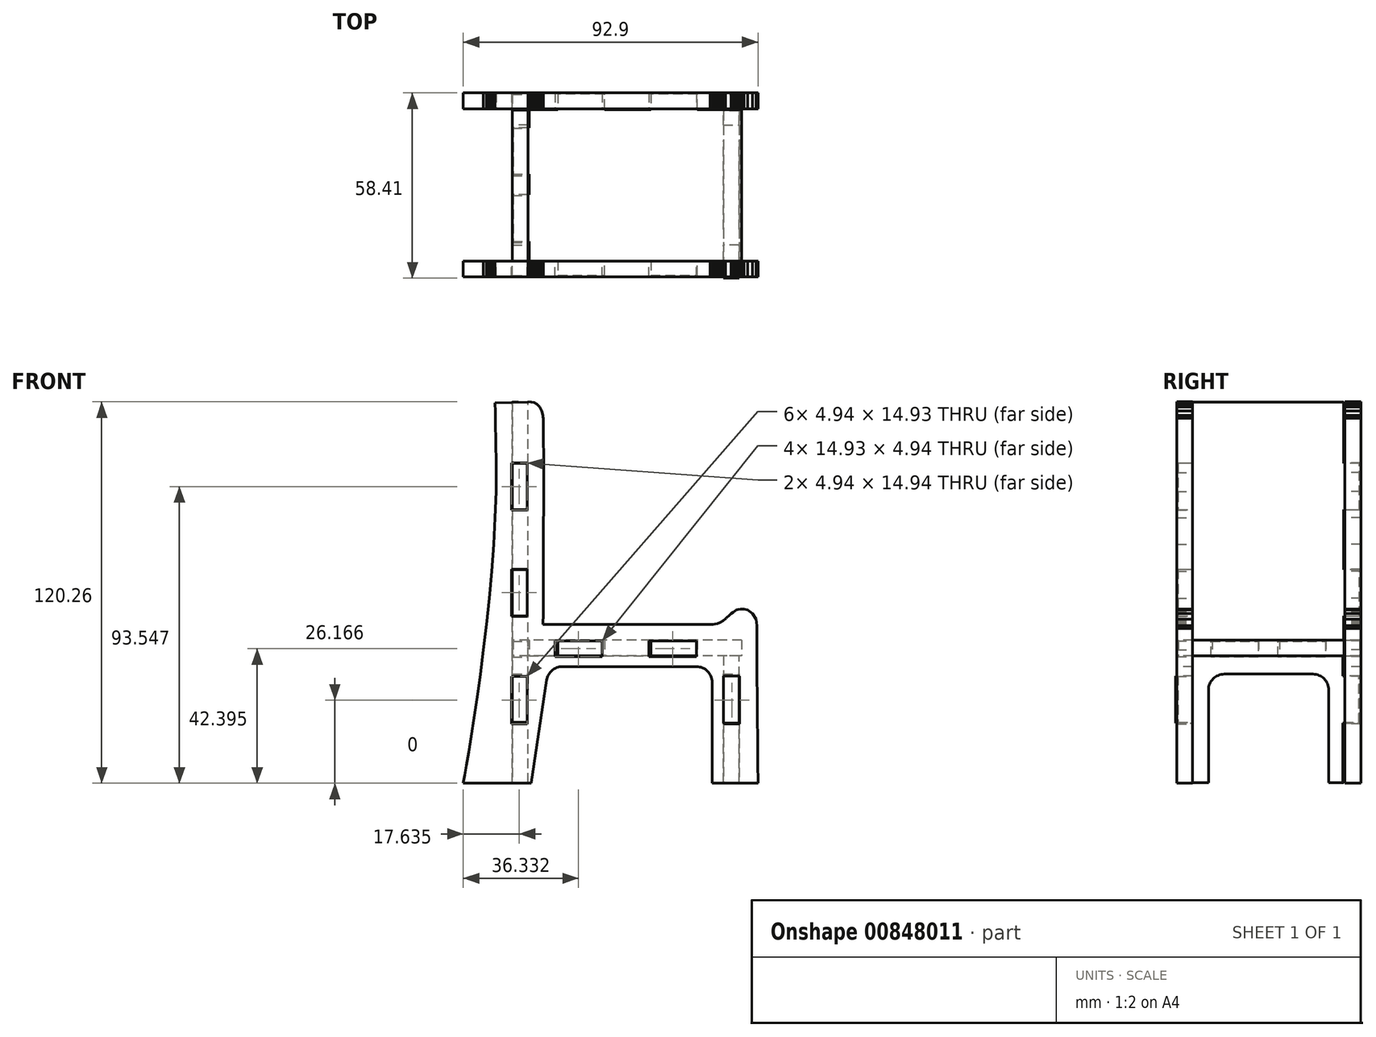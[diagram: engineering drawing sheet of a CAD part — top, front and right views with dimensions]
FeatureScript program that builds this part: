
annotation { "Feature Type Name" : "Feature", "Feature Type Description" : "" }
export const myFeature = defineFeature(function(context is Context, id is Id, definition is map)
    precondition{}
    {
        {
            var Q0;
            Q0=qCreatedBy(makeId("Front.planeOp"),FACE);
            var sketch = newSketch(context, id + "F0", { "sketchPlane" : qUnion([Q0])});
            skLineSegment(sketch, "E0", {"start": v(-31.28, -26.5) * mm, "end": v(-26.35, -26.5) * mm});
            skLineSegment(sketch, "E1", {"start": v(-26.35, -26.5) * mm, "end": v(-26.35, -41.43) * mm});
            skLineSegment(sketch, "E2", {"start": v(-26.35, -41.43) * mm, "end": v(-31.28, -41.43) * mm});
            skLineSegment(sketch, "E3", {"start": v(-31.28, -41.43) * mm, "end": v(-31.28, -26.5) * mm});
            skLineSegment(sketch, "E4", {"start": v(-31.28, 7.37) * mm, "end": v(-26.35, 7.37) * mm});
            skLineSegment(sketch, "E5", {"start": v(-26.35, 7.37) * mm, "end": v(-26.35, -7.56) * mm});
            skLineSegment(sketch, "E6", {"start": v(-26.35, -7.56) * mm, "end": v(-31.28, -7.56) * mm});
            skLineSegment(sketch, "E7", {"start": v(-31.28, -7.56) * mm, "end": v(-31.28, 7.37) * mm});
            skLineSegment(sketch, "E8", {"start": v(-31.28, 40.88) * mm, "end": v(-26.35, 40.88) * mm});
            skLineSegment(sketch, "E9", {"start": v(-26.35, 40.88) * mm, "end": v(-26.35, 25.95) * mm});
            skLineSegment(sketch, "E10", {"start": v(-26.35, 25.95) * mm, "end": v(-31.28, 25.95) * mm});
            skLineSegment(sketch, "E11", {"start": v(-31.28, 25.95) * mm, "end": v(-31.28, 40.88) * mm});
            skLineSegment(sketch, "E12", {"start": v(-17.59, -15.27) * mm, "end": v(-2.65, -15.27) * mm});
            skLineSegment(sketch, "E13", {"start": v(-2.65, -15.27) * mm, "end": v(-2.65, -20.2) * mm});
            skLineSegment(sketch, "E14", {"start": v(-2.65, -20.2) * mm, "end": v(-17.59, -20.2) * mm});
            skLineSegment(sketch, "E15", {"start": v(-17.59, -20.2) * mm, "end": v(-17.59, -15.27) * mm});
            skLineSegment(sketch, "E16", {"start": v(12.05, -15.27) * mm, "end": v(26.98, -15.27) * mm});
            skLineSegment(sketch, "E17", {"start": v(26.98, -15.27) * mm, "end": v(26.98, -20.2) * mm});
            skLineSegment(sketch, "E18", {"start": v(26.98, -20.2) * mm, "end": v(12.05, -20.2) * mm});
            skLineSegment(sketch, "E19", {"start": v(12.05, -20.2) * mm, "end": v(12.05, -15.27) * mm});
            skLineSegment(sketch, "E20", {"start": v(35.74, -26.5) * mm, "end": v(40.68, -26.5) * mm});
            skLineSegment(sketch, "E21", {"start": v(40.68, -26.5) * mm, "end": v(40.68, -41.43) * mm});
            skLineSegment(sketch, "E22", {"start": v(40.68, -41.43) * mm, "end": v(35.74, -41.43) * mm});
            skLineSegment(sketch, "E23", {"start": v(35.74, -41.43) * mm, "end": v(35.74, -26.5) * mm});
            skLineSegment(sketch, "E24", {"start": v(46.45, -60.13) * mm, "end": v(46.45, -59.6) * mm});
            skLineSegment(sketch, "E25", {"start": v(46.45, -59.6) * mm, "end": v(46.43, -58.1) * mm});
            skLineSegment(sketch, "E26", {"start": v(46.43, -58.1) * mm, "end": v(46.4, -55.78) * mm});
            skLineSegment(sketch, "E27", {"start": v(46.4, -55.78) * mm, "end": v(46.37, -52.76) * mm});
            skLineSegment(sketch, "E28", {"start": v(46.37, -52.76) * mm, "end": v(46.33, -49.18) * mm});
            skLineSegment(sketch, "E29", {"start": v(46.33, -49.18) * mm, "end": v(46.29, -45.17) * mm});
            skLineSegment(sketch, "E30", {"start": v(46.29, -45.17) * mm, "end": v(46.24, -40.87) * mm});
            skLineSegment(sketch, "E31", {"start": v(46.24, -40.87) * mm, "end": v(46.2, -36.4) * mm});
            skLineSegment(sketch, "E32", {"start": v(46.2, -36.4) * mm, "end": v(46.16, -31.92) * mm});
            skLineSegment(sketch, "E33", {"start": v(46.16, -31.92) * mm, "end": v(46.12, -27.54) * mm});
            skLineSegment(sketch, "E34", {"start": v(46.12, -27.54) * mm, "end": v(46.09, -23.4) * mm});
            skLineSegment(sketch, "E35", {"start": v(46.09, -23.4) * mm, "end": v(46.07, -19.65) * mm});
            skLineSegment(sketch, "E36", {"start": v(46.07, -19.65) * mm, "end": v(46.05, -16.4) * mm});
            skLineSegment(sketch, "E37", {"start": v(46.05, -16.4) * mm, "end": v(46.05, -13.8) * mm});
            skLineSegment(sketch, "E38", {"start": v(46.05, -13.8) * mm, "end": v(46.06, -12) * mm});
            skLineSegment(sketch, "E39", {"start": v(46.06, -12) * mm, "end": v(46.07, -11.32) * mm});
            skLineSegment(sketch, "E40", {"start": v(46.07, -11.32) * mm, "end": v(46.1, -11.1) * mm});
            skLineSegment(sketch, "E41", {"start": v(46.1, -11.1) * mm, "end": v(46.15, -10.45) * mm});
            skLineSegment(sketch, "E42", {"start": v(46.15, -10.45) * mm, "end": v(45.82, -8.46) * mm});
            skLineSegment(sketch, "E43", {"start": v(45.82, -8.46) * mm, "end": v(44.73, -6.62) * mm});
            skLineSegment(sketch, "E44", {"start": v(44.73, -6.62) * mm, "end": v(43.22, -5.54) * mm});
            skLineSegment(sketch, "E45", {"start": v(43.22, -5.54) * mm, "end": v(42.06, -5.2) * mm});
            skLineSegment(sketch, "E46", {"start": v(42.06, -5.2) * mm, "end": v(41.68, -5.21) * mm});
            skLineSegment(sketch, "E47", {"start": v(41.68, -5.21) * mm, "end": v(41.47, -5.22) * mm});
            skLineSegment(sketch, "E48", {"start": v(41.47, -5.22) * mm, "end": v(40.83, -5.27) * mm});
            skLineSegment(sketch, "E49", {"start": v(40.83, -5.27) * mm, "end": v(40.14, -5.37) * mm});
            skLineSegment(sketch, "E50", {"start": v(40.14, -5.37) * mm, "end": v(39.57, -5.56) * mm});
            skLineSegment(sketch, "E51", {"start": v(39.57, -5.56) * mm, "end": v(39.06, -5.83) * mm});
            skLineSegment(sketch, "E52", {"start": v(39.06, -5.83) * mm, "end": v(38.54, -6.2) * mm});
            skLineSegment(sketch, "E53", {"start": v(38.54, -6.2) * mm, "end": v(37.96, -6.7) * mm});
            skLineSegment(sketch, "E54", {"start": v(37.96, -6.7) * mm, "end": v(37.27, -7.34) * mm});
            skLineSegment(sketch, "E55", {"start": v(37.27, -7.34) * mm, "end": v(36.63, -7.94) * mm});
            skLineSegment(sketch, "E56", {"start": v(36.63, -7.94) * mm, "end": v(36.4, -8.14) * mm});
            skLineSegment(sketch, "E57", {"start": v(36.4, -8.14) * mm, "end": v(36.18, -8.34) * mm});
            skLineSegment(sketch, "E58", {"start": v(36.18, -8.34) * mm, "end": v(35.45, -8.9) * mm});
            skLineSegment(sketch, "E59", {"start": v(35.45, -8.9) * mm, "end": v(34.53, -9.43) * mm});
            skLineSegment(sketch, "E60", {"start": v(34.53, -9.43) * mm, "end": v(33.68, -9.77) * mm});
            skLineSegment(sketch, "E61", {"start": v(33.68, -9.77) * mm, "end": v(32.93, -9.97) * mm});
            skLineSegment(sketch, "E62", {"start": v(32.93, -9.97) * mm, "end": v(32.3, -10.05) * mm});
            skLineSegment(sketch, "E63", {"start": v(32.3, -10.05) * mm, "end": v(31.81, -10.07) * mm});
            skLineSegment(sketch, "E64", {"start": v(31.81, -10.07) * mm, "end": v(31.5, -10.05) * mm});
            skLineSegment(sketch, "E65", {"start": v(31.5, -10.05) * mm, "end": v(31.4, -10.03) * mm});
            skLineSegment(sketch, "E66", {"start": v(31.4, -10.03) * mm, "end": v(-21.29, -10.03) * mm});
            skLineSegment(sketch, "E67", {"start": v(-21.29, -10.03) * mm, "end": v(-21.29, -9.35) * mm});
            skLineSegment(sketch, "E68", {"start": v(-21.29, -9.35) * mm, "end": v(-21.28, -7.4) * mm});
            skLineSegment(sketch, "E69", {"start": v(-21.28, -7.4) * mm, "end": v(-21.26, -4.36) * mm});
            skLineSegment(sketch, "E70", {"start": v(-21.26, -4.36) * mm, "end": v(-21.24, -0.41) * mm});
            skLineSegment(sketch, "E71", {"start": v(-21.24, -0.41) * mm, "end": v(-21.22, 4.28) * mm});
            skLineSegment(sketch, "E72", {"start": v(-21.22, 4.28) * mm, "end": v(-21.2, 9.53) * mm});
            skLineSegment(sketch, "E73", {"start": v(-21.2, 9.53) * mm, "end": v(-21.18, 15.19) * mm});
            skLineSegment(sketch, "E74", {"start": v(-21.18, 15.19) * mm, "end": v(-21.16, 21.07) * mm});
            skLineSegment(sketch, "E75", {"start": v(-21.16, 21.07) * mm, "end": v(-21.15, 27) * mm});
            skLineSegment(sketch, "E76", {"start": v(-21.15, 27) * mm, "end": v(-21.14, 32.8) * mm});
            skLineSegment(sketch, "E77", {"start": v(-21.14, 32.8) * mm, "end": v(-21.14, 38.3) * mm});
            skLineSegment(sketch, "E78", {"start": v(-21.14, 38.3) * mm, "end": v(-21.14, 43.34) * mm});
            skLineSegment(sketch, "E79", {"start": v(-21.14, 43.34) * mm, "end": v(-21.16, 47.74) * mm});
            skLineSegment(sketch, "E80", {"start": v(-21.16, 47.74) * mm, "end": v(-21.2, 51.32) * mm});
            skLineSegment(sketch, "E81", {"start": v(-21.2, 51.32) * mm, "end": v(-21.23, 53.92) * mm});
            skLineSegment(sketch, "E82", {"start": v(-21.23, 53.92) * mm, "end": v(-21.26, 55) * mm});
            skLineSegment(sketch, "E83", {"start": v(-21.26, 55) * mm, "end": v(-21.29, 55.35) * mm});
            skLineSegment(sketch, "E84", {"start": v(-21.29, 55.35) * mm, "end": v(-21.33, 55.82) * mm});
            skLineSegment(sketch, "E85", {"start": v(-21.33, 55.82) * mm, "end": v(-21.66, 57.2) * mm});
            skLineSegment(sketch, "E86", {"start": v(-21.66, 57.2) * mm, "end": v(-22.35, 58.52) * mm});
            skLineSegment(sketch, "E87", {"start": v(-22.35, 58.52) * mm, "end": v(-23.21, 59.37) * mm});
            skLineSegment(sketch, "E88", {"start": v(-23.21, 59.37) * mm, "end": v(-24.14, 59.86) * mm});
            skLineSegment(sketch, "E89", {"start": v(-24.14, 59.86) * mm, "end": v(-25.01, 60.08) * mm});
            skLineSegment(sketch, "E90", {"start": v(-25.01, 60.08) * mm, "end": v(-25.7, 60.13) * mm});
            skLineSegment(sketch, "E91", {"start": v(-25.7, 60.13) * mm, "end": v(-26.06, 60.09) * mm});
            skLineSegment(sketch, "E92", {"start": v(-26.06, 60.09) * mm, "end": v(-26.01, 60.05) * mm});
            skLineSegment(sketch, "E93", {"start": v(-26.01, 60.05) * mm, "end": v(-26, 60.05) * mm});
            skLineSegment(sketch, "E94", {"start": v(-26, 60.05) * mm, "end": v(-36.43, 59.82) * mm});
            skLineSegment(sketch, "E95", {"start": v(-36.43, 59.82) * mm, "end": v(-36.42, 59.2) * mm});
            skLineSegment(sketch, "E96", {"start": v(-36.42, 59.2) * mm, "end": v(-36.39, 57.55) * mm});
            skLineSegment(sketch, "E97", {"start": v(-36.39, 57.55) * mm, "end": v(-36.35, 55.1) * mm});
            skLineSegment(sketch, "E98", {"start": v(-36.35, 55.1) * mm, "end": v(-36.3, 52.12) * mm});
            skLineSegment(sketch, "E99", {"start": v(-36.3, 52.12) * mm, "end": v(-36.24, 48.84) * mm});
            skLineSegment(sketch, "E100", {"start": v(-36.24, 48.84) * mm, "end": v(-36.19, 45.53) * mm});
            skLineSegment(sketch, "E101", {"start": v(-36.19, 45.53) * mm, "end": v(-36.14, 42.44) * mm});
            skLineSegment(sketch, "E102", {"start": v(-36.14, 42.44) * mm, "end": v(-36.11, 40.48) * mm});
            skLineSegment(sketch, "E103", {"start": v(-36.11, 40.48) * mm, "end": v(-36.1, 39.83) * mm});
            skLineSegment(sketch, "E104", {"start": v(-36.1, 39.83) * mm, "end": v(-36.08, 37.83) * mm});
            skLineSegment(sketch, "E105", {"start": v(-36.08, 37.83) * mm, "end": v(-36.14, 31.84) * mm});
            skLineSegment(sketch, "E106", {"start": v(-36.14, 31.84) * mm, "end": v(-36.4, 23.58) * mm});
            skLineSegment(sketch, "E107", {"start": v(-36.4, 23.58) * mm, "end": v(-36.87, 15.14) * mm});
            skLineSegment(sketch, "E108", {"start": v(-36.87, 15.14) * mm, "end": v(-37.5, 6.65) * mm});
            skLineSegment(sketch, "E109", {"start": v(-37.5, 6.65) * mm, "end": v(-38.28, -1.8) * mm});
            skLineSegment(sketch, "E110", {"start": v(-38.28, -1.8) * mm, "end": v(-39.16, -10.1) * mm});
            skLineSegment(sketch, "E111", {"start": v(-39.16, -10.1) * mm, "end": v(-40.1, -18.12) * mm});
            skLineSegment(sketch, "E112", {"start": v(-40.1, -18.12) * mm, "end": v(-41.09, -25.76) * mm});
            skLineSegment(sketch, "E113", {"start": v(-41.09, -25.76) * mm, "end": v(-42.08, -32.92) * mm});
            skLineSegment(sketch, "E114", {"start": v(-42.08, -32.92) * mm, "end": v(-43.05, -39.48) * mm});
            skLineSegment(sketch, "E115", {"start": v(-43.05, -39.48) * mm, "end": v(-43.95, -45.33) * mm});
            skLineSegment(sketch, "E116", {"start": v(-43.95, -45.33) * mm, "end": v(-44.77, -50.36) * mm});
            skLineSegment(sketch, "E117", {"start": v(-44.77, -50.36) * mm, "end": v(-45.46, -54.47) * mm});
            skLineSegment(sketch, "E118", {"start": v(-45.46, -54.47) * mm, "end": v(-46, -57.54) * mm});
            skLineSegment(sketch, "E119", {"start": v(-46, -57.54) * mm, "end": v(-46.33, -59.46) * mm});
            skLineSegment(sketch, "E120", {"start": v(-46.33, -59.46) * mm, "end": v(-46.45, -60.13) * mm});
            skLineSegment(sketch, "E121", {"start": v(-46.45, -60.13) * mm, "end": v(46.45, -60.13) * mm});
            skSolve(sketch);
        }
        {
            var Q0;
            Q0=makeQuery(id+"F0.imprint","IMPRINT",FACE,{"disambiguationData":[TD([[makeQuery(id+"F0.imprint","IMPRINT",EDGE,{"derivedFrom":sQuery(id+"F0.wireOp",EDGE,"E0")}),1.0]])]});
            extrude(context, id + "F1", {"entities" : qUnion([Q0]), "depth" : 5 * mm, "offsetDistance" : 25 * mm});
        }
        {
            var Q0;
            Q0=qCreatedBy(makeId("Front.planeOp"),FACE);
            cPlane(context, id + "F2", {"entities" : qUnion([Q0]), "cplaneType" : CPlaneType.OFFSET, "offset" : 48 * mm, "oppositeDirection" : true, "width" : 150 * mm, "height" : 150 * mm});
        }
        {
            var Q0;
            Q0=qCreatedBy(id+"F2.planeOp",FACE);
            var sketch = newSketch(context, id + "F3", { "sketchPlane" : qUnion([Q0])});
            skLineSegment(sketch, "E122", {"start": v(-31.28, -26.5) * mm, "end": v(-26.35, -26.5) * mm});
            skLineSegment(sketch, "E123", {"start": v(-26.35, -26.5) * mm, "end": v(-26.35, -41.43) * mm});
            skLineSegment(sketch, "E124", {"start": v(-26.35, -41.43) * mm, "end": v(-31.28, -41.43) * mm});
            skLineSegment(sketch, "E125", {"start": v(-31.28, -41.43) * mm, "end": v(-31.28, -26.5) * mm});
            skLineSegment(sketch, "E126", {"start": v(-31.28, 7.37) * mm, "end": v(-26.35, 7.37) * mm});
            skLineSegment(sketch, "E127", {"start": v(-26.35, 7.37) * mm, "end": v(-26.35, -7.56) * mm});
            skLineSegment(sketch, "E128", {"start": v(-26.35, -7.56) * mm, "end": v(-31.28, -7.56) * mm});
            skLineSegment(sketch, "E129", {"start": v(-31.28, -7.56) * mm, "end": v(-31.28, 7.37) * mm});
            skLineSegment(sketch, "E130", {"start": v(-31.28, 40.88) * mm, "end": v(-26.35, 40.88) * mm});
            skLineSegment(sketch, "E131", {"start": v(-26.35, 40.88) * mm, "end": v(-26.35, 25.95) * mm});
            skLineSegment(sketch, "E132", {"start": v(-26.35, 25.95) * mm, "end": v(-31.28, 25.95) * mm});
            skLineSegment(sketch, "E133", {"start": v(-31.28, 25.95) * mm, "end": v(-31.28, 40.88) * mm});
            skLineSegment(sketch, "E134", {"start": v(-17.59, -15.27) * mm, "end": v(-2.65, -15.27) * mm});
            skLineSegment(sketch, "E135", {"start": v(-2.65, -15.27) * mm, "end": v(-2.65, -20.2) * mm});
            skLineSegment(sketch, "E136", {"start": v(-2.65, -20.2) * mm, "end": v(-17.59, -20.2) * mm});
            skLineSegment(sketch, "E137", {"start": v(-17.59, -20.2) * mm, "end": v(-17.59, -15.27) * mm});
            skLineSegment(sketch, "E138", {"start": v(12.05, -15.27) * mm, "end": v(26.98, -15.27) * mm});
            skLineSegment(sketch, "E139", {"start": v(26.98, -15.27) * mm, "end": v(26.98, -20.2) * mm});
            skLineSegment(sketch, "E140", {"start": v(26.98, -20.2) * mm, "end": v(12.05, -20.2) * mm});
            skLineSegment(sketch, "E141", {"start": v(12.05, -20.2) * mm, "end": v(12.05, -15.27) * mm});
            skLineSegment(sketch, "E142", {"start": v(35.74, -26.5) * mm, "end": v(40.68, -26.5) * mm});
            skLineSegment(sketch, "E143", {"start": v(40.68, -26.5) * mm, "end": v(40.68, -41.43) * mm});
            skLineSegment(sketch, "E144", {"start": v(40.68, -41.43) * mm, "end": v(35.74, -41.43) * mm});
            skLineSegment(sketch, "E145", {"start": v(35.74, -41.43) * mm, "end": v(35.74, -26.5) * mm});
            skLineSegment(sketch, "E146", {"start": v(46.45, -60.13) * mm, "end": v(46.45, -59.6) * mm});
            skLineSegment(sketch, "E147", {"start": v(46.45, -59.6) * mm, "end": v(46.43, -58.1) * mm});
            skLineSegment(sketch, "E148", {"start": v(46.43, -58.1) * mm, "end": v(46.4, -55.78) * mm});
            skLineSegment(sketch, "E149", {"start": v(46.4, -55.78) * mm, "end": v(46.37, -52.76) * mm});
            skLineSegment(sketch, "E150", {"start": v(46.37, -52.76) * mm, "end": v(46.33, -49.18) * mm});
            skLineSegment(sketch, "E151", {"start": v(46.33, -49.18) * mm, "end": v(46.29, -45.17) * mm});
            skLineSegment(sketch, "E152", {"start": v(46.29, -45.17) * mm, "end": v(46.24, -40.87) * mm});
            skLineSegment(sketch, "E153", {"start": v(46.24, -40.87) * mm, "end": v(46.2, -36.4) * mm});
            skLineSegment(sketch, "E154", {"start": v(46.2, -36.4) * mm, "end": v(46.16, -31.92) * mm});
            skLineSegment(sketch, "E155", {"start": v(46.16, -31.92) * mm, "end": v(46.12, -27.54) * mm});
            skLineSegment(sketch, "E156", {"start": v(46.12, -27.54) * mm, "end": v(46.09, -23.4) * mm});
            skLineSegment(sketch, "E157", {"start": v(46.09, -23.4) * mm, "end": v(46.07, -19.65) * mm});
            skLineSegment(sketch, "E158", {"start": v(46.07, -19.65) * mm, "end": v(46.05, -16.4) * mm});
            skLineSegment(sketch, "E159", {"start": v(46.05, -16.4) * mm, "end": v(46.05, -13.8) * mm});
            skLineSegment(sketch, "E160", {"start": v(46.05, -13.8) * mm, "end": v(46.06, -12) * mm});
            skLineSegment(sketch, "E161", {"start": v(46.06, -12) * mm, "end": v(46.07, -11.32) * mm});
            skLineSegment(sketch, "E162", {"start": v(46.07, -11.32) * mm, "end": v(46.1, -11.1) * mm});
            skLineSegment(sketch, "E163", {"start": v(46.1, -11.1) * mm, "end": v(46.15, -10.45) * mm});
            skLineSegment(sketch, "E164", {"start": v(46.15, -10.45) * mm, "end": v(45.82, -8.46) * mm});
            skLineSegment(sketch, "E165", {"start": v(45.82, -8.46) * mm, "end": v(44.73, -6.62) * mm});
            skLineSegment(sketch, "E166", {"start": v(44.73, -6.62) * mm, "end": v(43.22, -5.54) * mm});
            skLineSegment(sketch, "E167", {"start": v(43.22, -5.54) * mm, "end": v(42.06, -5.2) * mm});
            skLineSegment(sketch, "E168", {"start": v(42.06, -5.2) * mm, "end": v(41.68, -5.21) * mm});
            skLineSegment(sketch, "E169", {"start": v(41.68, -5.21) * mm, "end": v(41.47, -5.22) * mm});
            skLineSegment(sketch, "E170", {"start": v(41.47, -5.22) * mm, "end": v(40.83, -5.27) * mm});
            skLineSegment(sketch, "E171", {"start": v(40.83, -5.27) * mm, "end": v(40.14, -5.37) * mm});
            skLineSegment(sketch, "E172", {"start": v(40.14, -5.37) * mm, "end": v(39.57, -5.56) * mm});
            skLineSegment(sketch, "E173", {"start": v(39.57, -5.56) * mm, "end": v(39.06, -5.83) * mm});
            skLineSegment(sketch, "E174", {"start": v(39.06, -5.83) * mm, "end": v(38.54, -6.2) * mm});
            skLineSegment(sketch, "E175", {"start": v(38.54, -6.2) * mm, "end": v(37.96, -6.7) * mm});
            skLineSegment(sketch, "E176", {"start": v(37.96, -6.7) * mm, "end": v(37.27, -7.34) * mm});
            skLineSegment(sketch, "E177", {"start": v(37.27, -7.34) * mm, "end": v(36.63, -7.94) * mm});
            skLineSegment(sketch, "E178", {"start": v(36.63, -7.94) * mm, "end": v(36.4, -8.14) * mm});
            skLineSegment(sketch, "E179", {"start": v(36.4, -8.14) * mm, "end": v(36.18, -8.34) * mm});
            skLineSegment(sketch, "E180", {"start": v(36.18, -8.34) * mm, "end": v(35.45, -8.9) * mm});
            skLineSegment(sketch, "E181", {"start": v(35.45, -8.9) * mm, "end": v(34.53, -9.43) * mm});
            skLineSegment(sketch, "E182", {"start": v(34.53, -9.43) * mm, "end": v(33.68, -9.77) * mm});
            skLineSegment(sketch, "E183", {"start": v(33.68, -9.77) * mm, "end": v(32.93, -9.97) * mm});
            skLineSegment(sketch, "E184", {"start": v(32.93, -9.97) * mm, "end": v(32.3, -10.05) * mm});
            skLineSegment(sketch, "E185", {"start": v(32.3, -10.05) * mm, "end": v(31.81, -10.07) * mm});
            skLineSegment(sketch, "E186", {"start": v(31.81, -10.07) * mm, "end": v(31.5, -10.05) * mm});
            skLineSegment(sketch, "E187", {"start": v(31.5, -10.05) * mm, "end": v(31.4, -10.03) * mm});
            skLineSegment(sketch, "E188", {"start": v(31.4, -10.03) * mm, "end": v(-21.29, -10.03) * mm});
            skLineSegment(sketch, "E189", {"start": v(-21.29, -10.03) * mm, "end": v(-21.29, -9.35) * mm});
            skLineSegment(sketch, "E190", {"start": v(-21.29, -9.35) * mm, "end": v(-21.28, -7.4) * mm});
            skLineSegment(sketch, "E191", {"start": v(-21.28, -7.4) * mm, "end": v(-21.26, -4.36) * mm});
            skLineSegment(sketch, "E192", {"start": v(-21.26, -4.36) * mm, "end": v(-21.24, -0.41) * mm});
            skLineSegment(sketch, "E193", {"start": v(-21.24, -0.41) * mm, "end": v(-21.22, 4.28) * mm});
            skLineSegment(sketch, "E194", {"start": v(-21.22, 4.28) * mm, "end": v(-21.2, 9.53) * mm});
            skLineSegment(sketch, "E195", {"start": v(-21.2, 9.53) * mm, "end": v(-21.18, 15.19) * mm});
            skLineSegment(sketch, "E196", {"start": v(-21.18, 15.19) * mm, "end": v(-21.16, 21.07) * mm});
            skLineSegment(sketch, "E197", {"start": v(-21.16, 21.07) * mm, "end": v(-21.15, 27) * mm});
            skLineSegment(sketch, "E198", {"start": v(-21.15, 27) * mm, "end": v(-21.14, 32.8) * mm});
            skLineSegment(sketch, "E199", {"start": v(-21.14, 32.8) * mm, "end": v(-21.14, 38.3) * mm});
            skLineSegment(sketch, "E200", {"start": v(-21.14, 38.3) * mm, "end": v(-21.14, 43.34) * mm});
            skLineSegment(sketch, "E201", {"start": v(-21.14, 43.34) * mm, "end": v(-21.16, 47.74) * mm});
            skLineSegment(sketch, "E202", {"start": v(-21.16, 47.74) * mm, "end": v(-21.2, 51.32) * mm});
            skLineSegment(sketch, "E203", {"start": v(-21.2, 51.32) * mm, "end": v(-21.23, 53.92) * mm});
            skLineSegment(sketch, "E204", {"start": v(-21.23, 53.92) * mm, "end": v(-21.26, 55) * mm});
            skLineSegment(sketch, "E205", {"start": v(-21.26, 55) * mm, "end": v(-21.29, 55.35) * mm});
            skLineSegment(sketch, "E206", {"start": v(-21.29, 55.35) * mm, "end": v(-21.33, 55.82) * mm});
            skLineSegment(sketch, "E207", {"start": v(-21.33, 55.82) * mm, "end": v(-21.66, 57.2) * mm});
            skLineSegment(sketch, "E208", {"start": v(-21.66, 57.2) * mm, "end": v(-22.35, 58.52) * mm});
            skLineSegment(sketch, "E209", {"start": v(-22.35, 58.52) * mm, "end": v(-23.21, 59.37) * mm});
            skLineSegment(sketch, "E210", {"start": v(-23.21, 59.37) * mm, "end": v(-24.14, 59.86) * mm});
            skLineSegment(sketch, "E211", {"start": v(-24.14, 59.86) * mm, "end": v(-25.01, 60.08) * mm});
            skLineSegment(sketch, "E212", {"start": v(-25.01, 60.08) * mm, "end": v(-25.7, 60.13) * mm});
            skLineSegment(sketch, "E213", {"start": v(-25.7, 60.13) * mm, "end": v(-26.06, 60.09) * mm});
            skLineSegment(sketch, "E214", {"start": v(-26.06, 60.09) * mm, "end": v(-26.01, 60.05) * mm});
            skLineSegment(sketch, "E215", {"start": v(-26.01, 60.05) * mm, "end": v(-26, 60.05) * mm});
            skLineSegment(sketch, "E216", {"start": v(-26, 60.05) * mm, "end": v(-36.43, 59.82) * mm});
            skLineSegment(sketch, "E217", {"start": v(-36.43, 59.82) * mm, "end": v(-36.42, 59.2) * mm});
            skLineSegment(sketch, "E218", {"start": v(-36.42, 59.2) * mm, "end": v(-36.39, 57.55) * mm});
            skLineSegment(sketch, "E219", {"start": v(-36.39, 57.55) * mm, "end": v(-36.35, 55.1) * mm});
            skLineSegment(sketch, "E220", {"start": v(-36.35, 55.1) * mm, "end": v(-36.3, 52.12) * mm});
            skLineSegment(sketch, "E221", {"start": v(-36.3, 52.12) * mm, "end": v(-36.24, 48.84) * mm});
            skLineSegment(sketch, "E222", {"start": v(-36.24, 48.84) * mm, "end": v(-36.19, 45.53) * mm});
            skLineSegment(sketch, "E223", {"start": v(-36.19, 45.53) * mm, "end": v(-36.14, 42.44) * mm});
            skLineSegment(sketch, "E224", {"start": v(-36.14, 42.44) * mm, "end": v(-36.11, 40.48) * mm});
            skLineSegment(sketch, "E225", {"start": v(-36.11, 40.48) * mm, "end": v(-36.1, 39.83) * mm});
            skLineSegment(sketch, "E226", {"start": v(-36.1, 39.83) * mm, "end": v(-36.08, 37.83) * mm});
            skLineSegment(sketch, "E227", {"start": v(-36.08, 37.83) * mm, "end": v(-36.14, 31.84) * mm});
            skLineSegment(sketch, "E228", {"start": v(-36.14, 31.84) * mm, "end": v(-36.4, 23.58) * mm});
            skLineSegment(sketch, "E229", {"start": v(-36.4, 23.58) * mm, "end": v(-36.87, 15.14) * mm});
            skLineSegment(sketch, "E230", {"start": v(-36.87, 15.14) * mm, "end": v(-37.5, 6.65) * mm});
            skLineSegment(sketch, "E231", {"start": v(-37.5, 6.65) * mm, "end": v(-38.28, -1.8) * mm});
            skLineSegment(sketch, "E232", {"start": v(-38.28, -1.8) * mm, "end": v(-39.16, -10.1) * mm});
            skLineSegment(sketch, "E233", {"start": v(-39.16, -10.1) * mm, "end": v(-40.1, -18.12) * mm});
            skLineSegment(sketch, "E234", {"start": v(-40.1, -18.12) * mm, "end": v(-41.09, -25.76) * mm});
            skLineSegment(sketch, "E235", {"start": v(-41.09, -25.76) * mm, "end": v(-42.08, -32.92) * mm});
            skLineSegment(sketch, "E236", {"start": v(-42.08, -32.92) * mm, "end": v(-43.05, -39.48) * mm});
            skLineSegment(sketch, "E237", {"start": v(-43.05, -39.48) * mm, "end": v(-43.95, -45.33) * mm});
            skLineSegment(sketch, "E238", {"start": v(-43.95, -45.33) * mm, "end": v(-44.77, -50.36) * mm});
            skLineSegment(sketch, "E239", {"start": v(-44.77, -50.36) * mm, "end": v(-45.46, -54.47) * mm});
            skLineSegment(sketch, "E240", {"start": v(-45.46, -54.47) * mm, "end": v(-46, -57.54) * mm});
            skLineSegment(sketch, "E241", {"start": v(-46, -57.54) * mm, "end": v(-46.33, -59.46) * mm});
            skLineSegment(sketch, "E242", {"start": v(-46.33, -59.46) * mm, "end": v(-46.45, -60.13) * mm});
            skLineSegment(sketch, "E243", {"start": v(-46.45, -60.13) * mm, "end": v(46.45, -60.13) * mm});
            skSolve(sketch);
        }
        {
            var Q0;
            Q0=makeQuery(id+"F3.imprint","IMPRINT",FACE,{"disambiguationData":[TD([[makeQuery(id+"F3.imprint","IMPRINT",EDGE,{"derivedFrom":sQuery(id+"F3.wireOp",EDGE,"E122")}),1.0]])]});
            extrude(context, id + "F4", {"entities" : qUnion([Q0]), "oppositeDirection" : true, "depth" : 5 * mm, "offsetDistance" : 25 * mm});
        }
        {
            var Q0;
            Q0=qCreatedBy(makeId("Right.planeOp"),FACE);
            cPlane(context, id + "F5", {"entities" : qUnion([Q0]), "cplaneType" : CPlaneType.OFFSET, "offset" : 26 * mm, "oppositeDirection" : true, "width" : 150 * mm, "height" : 150 * mm});
        }
        {
            var Q0;
            Q0=qCreatedBy(id+"F5.planeOp",FACE);
            var sketch = newSketch(context, id + "F6", { "sketchPlane" : qUnion([Q0])});
            skLineSegment(sketch, "E244", {"start": v(26.93, -15.41) * mm, "end": v(41.86, -15.41) * mm});
            skLineSegment(sketch, "E245", {"start": v(41.86, -15.41) * mm, "end": v(41.86, -20.35) * mm});
            skLineSegment(sketch, "E246", {"start": v(41.86, -20.35) * mm, "end": v(26.93, -20.35) * mm});
            skLineSegment(sketch, "E247", {"start": v(26.93, -20.35) * mm, "end": v(26.93, -15.41) * mm});
            skLineSegment(sketch, "E248", {"start": v(5.76, -15.41) * mm, "end": v(20.7, -15.41) * mm});
            skLineSegment(sketch, "E249", {"start": v(20.7, -15.41) * mm, "end": v(20.7, -20.35) * mm});
            skLineSegment(sketch, "E250", {"start": v(20.7, -20.35) * mm, "end": v(5.76, -20.35) * mm});
            skLineSegment(sketch, "E251", {"start": v(5.76, -20.35) * mm, "end": v(5.76, -15.41) * mm});
            skLineSegment(sketch, "E252", {"start": v(47.62, -40.93) * mm, "end": v(52.56, -40.93) * mm});
            skLineSegment(sketch, "E253", {"start": v(52.56, -40.93) * mm, "end": v(52.56, -26.3) * mm});
            skLineSegment(sketch, "E254", {"start": v(52.56, -26.3) * mm, "end": v(47.63, -26.3) * mm});
            skLineSegment(sketch, "E255", {"start": v(47.62, -26.3) * mm, "end": v(47.62, -7.42) * mm});
            skLineSegment(sketch, "E256", {"start": v(47.62, -7.42) * mm, "end": v(52.56, -7.42) * mm});
            skLineSegment(sketch, "E257", {"start": v(52.56, -7.42) * mm, "end": v(52.56, 7.22) * mm});
            skLineSegment(sketch, "E258", {"start": v(52.56, 7.22) * mm, "end": v(47.63, 7.22) * mm});
            skLineSegment(sketch, "E259", {"start": v(47.62, 7.22) * mm, "end": v(47.62, 26.1) * mm});
            skLineSegment(sketch, "E260", {"start": v(47.62, 26.1) * mm, "end": v(52.56, 26.1) * mm});
            skLineSegment(sketch, "E261", {"start": v(52.56, 26.1) * mm, "end": v(52.56, 40.74) * mm});
            skLineSegment(sketch, "E262", {"start": v(52.56, 40.74) * mm, "end": v(47.63, 40.74) * mm});
            skLineSegment(sketch, "E263", {"start": v(47.62, 40.74) * mm, "end": v(47.62, 59.98) * mm});
            skLineSegment(sketch, "E264", {"start": v(47.62, 59.98) * mm, "end": v(0, 59.98) * mm});
            skLineSegment(sketch, "E265", {"start": v(0, 59.98) * mm, "end": v(0, 40.74) * mm});
            skLineSegment(sketch, "E266", {"start": v(0, 40.74) * mm, "end": v(-4.59, 40.74) * mm});
            skLineSegment(sketch, "E267", {"start": v(-4.59, 40.74) * mm, "end": v(-4.59, 26.1) * mm});
            skLineSegment(sketch, "E268", {"start": v(-4.59, 26.1) * mm, "end": v(0, 26.1) * mm});
            skLineSegment(sketch, "E269", {"start": v(0, 26.1) * mm, "end": v(0, 7.22) * mm});
            skLineSegment(sketch, "E270", {"start": v(0, 7.22) * mm, "end": v(-4.59, 7.22) * mm});
            skLineSegment(sketch, "E271", {"start": v(-4.59, 7.22) * mm, "end": v(-4.59, -7.42) * mm});
            skLineSegment(sketch, "E272", {"start": v(-4.59, -7.42) * mm, "end": v(0, -7.42) * mm});
            skLineSegment(sketch, "E273", {"start": v(0, -7.42) * mm, "end": v(0, -26.3) * mm});
            skLineSegment(sketch, "E274", {"start": v(0, -26.3) * mm, "end": v(-4.59, -26.3) * mm});
            skLineSegment(sketch, "E275", {"start": v(-4.59, -26.3) * mm, "end": v(-4.59, -40.93) * mm});
            skLineSegment(sketch, "E276", {"start": v(-4.59, -40.93) * mm, "end": v(0, -40.93) * mm});
            skLineSegment(sketch, "E277", {"start": v(0, -40.93) * mm, "end": v(0, -59.98) * mm});
            skLineSegment(sketch, "E278", {"start": v(0, -59.98) * mm, "end": v(47.62, -59.98) * mm});
            skLineSegment(sketch, "E279", {"start": v(47.62, -59.98) * mm, "end": v(47.62, -40.93) * mm});
            skSolve(sketch);
        }
        {
            var Q0;
            Q0=makeQuery(id+"F6.imprint","IMPRINT",FACE,{"disambiguationData":[TD([[makeQuery(id+"F6.imprint","IMPRINT",EDGE,{"derivedFrom":sQuery(id+"F6.wireOp",EDGE,"E244")}),1.0]])]});
            extrude(context, id + "F7", {"entities" : qUnion([Q0]), "oppositeDirection" : true, "depth" : 5 * mm, "offsetDistance" : 25 * mm});
        }
        {
            var Q0;
            Q0=qCreatedBy(makeId("Top.planeOp"),FACE);
            cPlane(context, id + "F8", {"entities" : qUnion([Q0]), "cplaneType" : CPlaneType.OFFSET, "offset" : 20 * mm, "oppositeDirection" : true, "width" : 150 * mm, "height" : 150 * mm});
        }
        {
            var Q0;
            Q0=qCreatedBy(id+"F8.planeOp",FACE);
            var sketch = newSketch(context, id + "F9", { "sketchPlane" : qUnion([Q0])});
            skLineSegment(sketch, "E280", {"start": v(41.3, 47.74) * mm, "end": v(27.31, 47.74) * mm});
            skLineSegment(sketch, "E281", {"start": v(27.31, 47.74) * mm, "end": v(27.31, 52.68) * mm});
            skLineSegment(sketch, "E282", {"start": v(27.31, 52.68) * mm, "end": v(12.67, 52.68) * mm});
            skLineSegment(sketch, "E283", {"start": v(12.67, 52.68) * mm, "end": v(12.67, 47.74) * mm});
            skLineSegment(sketch, "E284", {"start": v(12.67, 47.74) * mm, "end": v(-1.97, 47.74) * mm});
            skLineSegment(sketch, "E285", {"start": v(-1.97, 47.74) * mm, "end": v(-1.97, 52.68) * mm});
            skLineSegment(sketch, "E286", {"start": v(-1.97, 52.68) * mm, "end": v(-16.6, 52.68) * mm});
            skLineSegment(sketch, "E287", {"start": v(-16.6, 52.68) * mm, "end": v(-16.6, 47.74) * mm});
            skLineSegment(sketch, "E288", {"start": v(-16.6, 47.74) * mm, "end": v(-25.72, 47.74) * mm});
            skLineSegment(sketch, "E289", {"start": v(-25.72, 47.74) * mm, "end": v(-25.72, 42) * mm});
            skLineSegment(sketch, "E290", {"start": v(-25.72, 42) * mm, "end": v(-30.8, 42) * mm});
            skLineSegment(sketch, "E291", {"start": v(-30.8, 42) * mm, "end": v(-30.8, 27.37) * mm});
            skLineSegment(sketch, "E292", {"start": v(-30.8, 27.37) * mm, "end": v(-25.72, 27.37) * mm});
            skLineSegment(sketch, "E293", {"start": v(-25.72, 27.37) * mm, "end": v(-25.72, 20.84) * mm});
            skLineSegment(sketch, "E294", {"start": v(-25.72, 20.84) * mm, "end": v(-30.8, 20.84) * mm});
            skLineSegment(sketch, "E295", {"start": v(-30.8, 20.84) * mm, "end": v(-30.8, 6.2) * mm});
            skLineSegment(sketch, "E296", {"start": v(-30.8, 6.2) * mm, "end": v(-25.72, 6.2) * mm});
            skLineSegment(sketch, "E297", {"start": v(-25.72, 6.2) * mm, "end": v(-25.72, 0) * mm});
            skLineSegment(sketch, "E298", {"start": v(-25.72, 0) * mm, "end": v(-16.6, 0) * mm});
            skLineSegment(sketch, "E299", {"start": v(-16.6, 0) * mm, "end": v(-16.6, -4.47) * mm});
            skLineSegment(sketch, "E300", {"start": v(-16.6, -4.47) * mm, "end": v(-1.97, -4.47) * mm});
            skLineSegment(sketch, "E301", {"start": v(-1.97, -4.47) * mm, "end": v(-1.97, 0) * mm});
            skLineSegment(sketch, "E302", {"start": v(-1.97, 0) * mm, "end": v(12.67, 0) * mm});
            skLineSegment(sketch, "E303", {"start": v(12.67, 0) * mm, "end": v(12.67, -4.47) * mm});
            skLineSegment(sketch, "E304", {"start": v(12.67, -4.47) * mm, "end": v(27.31, -4.47) * mm});
            skLineSegment(sketch, "E305", {"start": v(27.31, -4.47) * mm, "end": v(27.31, 0) * mm});
            skLineSegment(sketch, "E306", {"start": v(27.31, 0) * mm, "end": v(41.3, 0) * mm});
            skLineSegment(sketch, "E307", {"start": v(41.3, 0) * mm, "end": v(41.3, 47.74) * mm});
            skSolve(sketch);
        }
        {
            var Q0;
            Q0=makeQuery(id+"F9.imprint","IMPRINT",FACE,{"disambiguationData":[TD([[makeQuery(id+"F9.imprint","IMPRINT",EDGE,{"derivedFrom":sQuery(id+"F9.wireOp",EDGE,"E280")}),1.0]])]});
            extrude(context, id + "F10", {"entities" : qUnion([Q0]), "depth" : 5 * mm, "offsetDistance" : 25 * mm});
        }
        {
            var Q0;
            Q0=qCreatedBy(makeId("Right.planeOp"),FACE);
            cPlane(context, id + "F11", {"entities" : qUnion([Q0]), "cplaneType" : CPlaneType.OFFSET, "offset" : 35.5 * mm, "width" : 150 * mm, "height" : 150 * mm});
        }
        {
            var Q0;
            Q0=qCreatedBy(id+"F11.planeOp",FACE);
            var sketch = newSketch(context, id + "F12", { "sketchPlane" : qUnion([Q0])});
            skLineSegment(sketch, "E308", {"start": v(52.45, -26.36) * mm, "end": v(47.27, -26.36) * mm});
            skLineSegment(sketch, "E309", {"start": v(47.27, -26.36) * mm, "end": v(47.27, -20) * mm});
            skLineSegment(sketch, "E310", {"start": v(47.27, -20) * mm, "end": v(0, -20) * mm});
            skLineSegment(sketch, "E311", {"start": v(0, -20) * mm, "end": v(0, -26.36) * mm});
            skLineSegment(sketch, "E312", {"start": v(0, -26.36) * mm, "end": v(-5.4, -26.36) * mm});
            skLineSegment(sketch, "E313", {"start": v(-5.4, -26.36) * mm, "end": v(-5.4, -41.18) * mm});
            skLineSegment(sketch, "E314", {"start": v(-5.4, -41.18) * mm, "end": v(0, -41.18) * mm});
            skLineSegment(sketch, "E315", {"start": v(0, -41.18) * mm, "end": v(0, -60) * mm});
            skLineSegment(sketch, "E316", {"start": v(0, -60) * mm, "end": v(47.27, -60) * mm});
            skLineSegment(sketch, "E317", {"start": v(47.27, -60) * mm, "end": v(47.27, -41.18) * mm});
            skLineSegment(sketch, "E318", {"start": v(47.27, -41.18) * mm, "end": v(52.45, -41.18) * mm});
            skLineSegment(sketch, "E319", {"start": v(52.45, -41.18) * mm, "end": v(52.45, -26.36) * mm});
            skSolve(sketch);
        }
        {
            var Q0;
            Q0=makeQuery(id+"F12.imprint","IMPRINT",FACE,{"disambiguationData":[TD([[makeQuery(id+"F12.imprint","IMPRINT",EDGE,{"derivedFrom":sQuery(id+"F12.wireOp",EDGE,"E308")}),1.0]])]});
            extrude(context, id + "F13", {"entities" : qUnion([Q0]), "depth" : 5 * mm, "offsetDistance" : 25 * mm});
        }
        {
            var Q0;
            Q0=qCreatedBy(makeId("Front.planeOp"),FACE);
            var sketch = newSketch(context, id + "F14", { "sketchPlane" : qUnion([Q0])});
            skLineSegment(sketch, "E320", {"start": v(-25.06, -60.03) * mm, "end": v(-20.16, -27.63) * mm});
            skLineSegment(sketch, "E321", {"start": v(-15.21, -23.38) * mm, "end": v(27, -23.38) * mm});
            skLineSegment(sketch, "E322", {"start": v(32, -28.38) * mm, "end": v(32, -60.03) * mm});
            skLineSegment(sketch, "E323", {"start": v(32, -60.03) * mm, "end": v(32, -66.96) * mm});
            skLineSegment(sketch, "E324", {"start": v(32, -66.96) * mm, "end": v(-25.06, -66.96) * mm});
            skLineSegment(sketch, "E325", {"start": v(-25.06, -66.96) * mm, "end": v(-25.06, -60.03) * mm});
            skPoint(sketch, "E326.visualSharp", {"position": v(-19.51, -23.38) * mm});
            skArc(sketch, "E326.filletArc", {"start": v(-15.21, -23.38) * mm, "mid": v(-18.47, -24.59) * mm, "end": v(-20.16, -27.63) * mm});
            skPoint(sketch, "E327.visualSharp", {"position": v(32, -23.38) * mm});
            skArc(sketch, "E327.filletArc", {"start": v(32, -28.38) * mm, "mid": v(30.53, -24.84) * mm, "end": v(27, -23.38) * mm});
            skSolve(sketch);
        }
        {
            var Q0;
            Q0=makeQuery(id+"F14.imprint","IMPRINT",FACE,{"disambiguationData":[TD([[makeQuery(id+"F14.imprint","IMPRINT",EDGE,{"derivedFrom":sQuery(id+"F14.wireOp",EDGE,"E320")}),-1.0]])]});
            extrude(context, id + "F15", {"entities" : qUnion([Q0]), "operationType" : NewBodyOperationType.REMOVE, "endBound" : BoundingType.SYMMETRIC, "oppositeDirection" : true, "depth" : 150 * mm, "offsetDistance" : 25 * mm});
        }
        {
            var Q0;
            Q0=qCreatedBy(makeId("Right.planeOp"),FACE);
            var sketch = newSketch(context, id + "F16", { "sketchPlane" : qUnion([Q0])});
            skLineSegment(sketch, "E328", {"start": v(5, -62.08) * mm, "end": v(5, -30.75) * mm});
            skLineSegment(sketch, "E329", {"start": v(10, -25.75) * mm, "end": v(37.92, -25.75) * mm});
            skLineSegment(sketch, "E330", {"start": v(42.92, -30.75) * mm, "end": v(42.92, -62.08) * mm});
            skLineSegment(sketch, "E331", {"start": v(42.92, -62.08) * mm, "end": v(5, -62.08) * mm});
            skPoint(sketch, "E332.visualSharp", {"position": v(5, -25.75) * mm});
            skArc(sketch, "E332.filletArc", {"start": v(10, -25.75) * mm, "mid": v(6.46, -27.22) * mm, "end": v(5, -30.75) * mm});
            skPoint(sketch, "E333.visualSharp", {"position": v(42.92, -25.75) * mm});
            skArc(sketch, "E333.filletArc", {"start": v(42.92, -30.75) * mm, "mid": v(41.45, -27.22) * mm, "end": v(37.92, -25.75) * mm});
            skSolve(sketch);
        }
        {
            var Q0;
            Q0=makeQuery(id+"F16.imprint","IMPRINT",FACE,{"disambiguationData":[TD([[makeQuery(id+"F16.imprint","IMPRINT",EDGE,{"derivedFrom":sQuery(id+"F16.wireOp",EDGE,"E328")}),-1.0]])]});
            extrude(context, id + "F17", {"entities" : qUnion([Q0]), "operationType" : NewBodyOperationType.REMOVE, "endBound" : BoundingType.SYMMETRIC, "oppositeDirection" : true, "depth" : 150 * mm, "offsetDistance" : 25 * mm});
        }
    });
